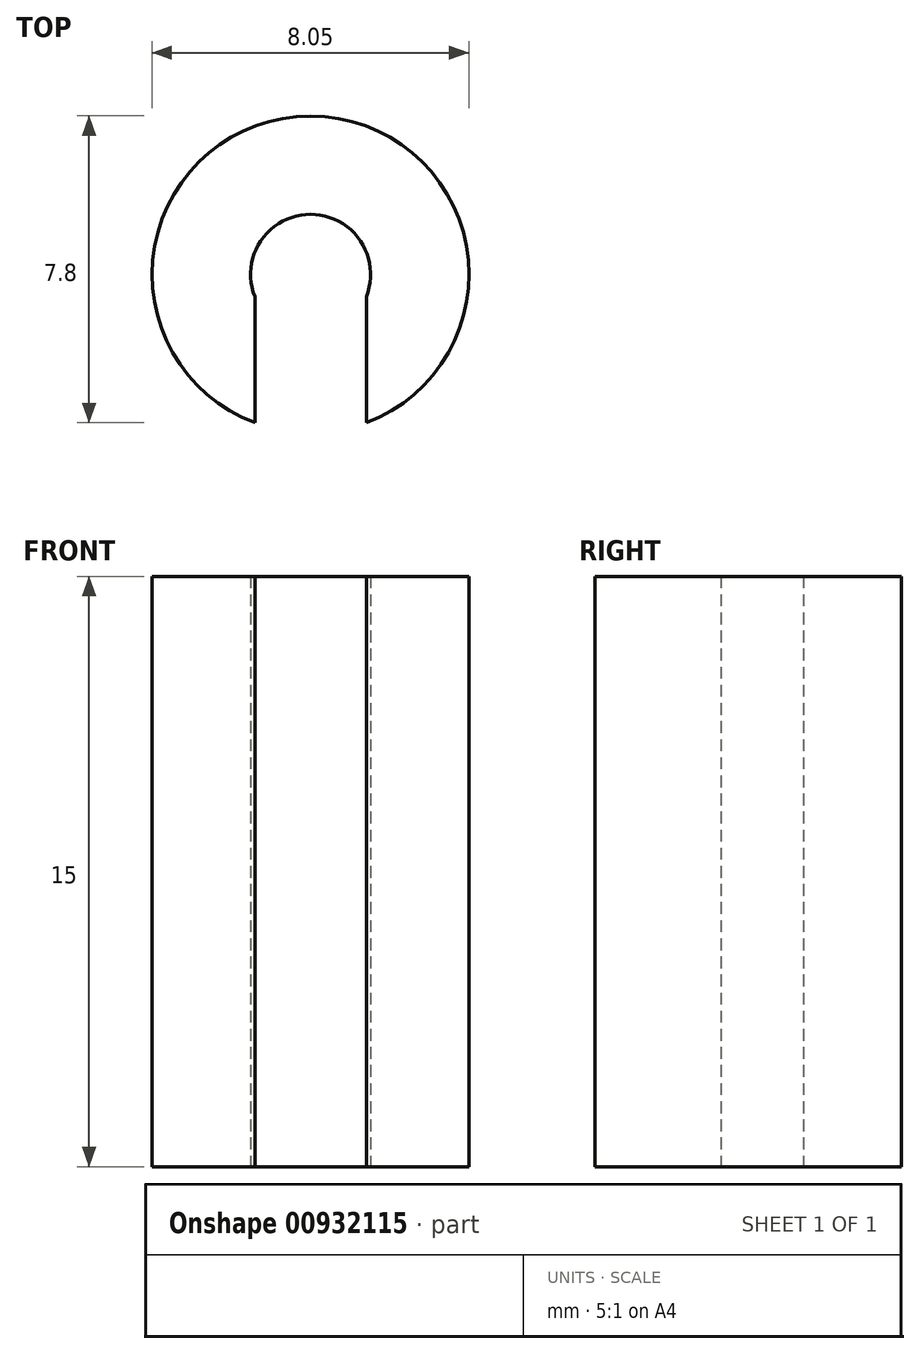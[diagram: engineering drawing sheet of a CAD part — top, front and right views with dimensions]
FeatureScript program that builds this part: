
annotation { "Feature Type Name" : "Feature", "Feature Type Description" : "" }
export const myFeature = defineFeature(function(context is Context, id is Id, definition is map)
    precondition{}
    {
        {
            var Q0;
            Q0=qCreatedBy(makeId("Top.planeOp"),FACE);
            var sketch = newSketch(context, id + "F0", { "sketchPlane" : qUnion([Q0])});
            skArc(sketch, "E0", {"start": v(1.42, -0.57) * mm, "mid": v(0, 1.53) * mm, "end": v(-1.42, -0.57) * mm});
            skArc(sketch, "E1", {"start": v(1.42, -3.77) * mm, "mid": v(0, 4.03) * mm, "end": v(-1.42, -3.77) * mm});
            skLineSegment(sketch, "E2", {"start": v(-1.42, -0.57) * mm, "end": v(-1.42, -3.77) * mm});
            skLineSegment(sketch, "E3", {"start": v(1.42, -0.57) * mm, "end": v(1.42, -3.77) * mm});
            skSolve(sketch);
        }
        {
            var Q0;
            Q0 = qSketchRegion(id + "F0", true);
            extrude(context, id + "F1", {"entities" : qUnion([Q0]), "depth" : 15 * mm, "offsetDistance" : 25 * mm});
        }
    });
